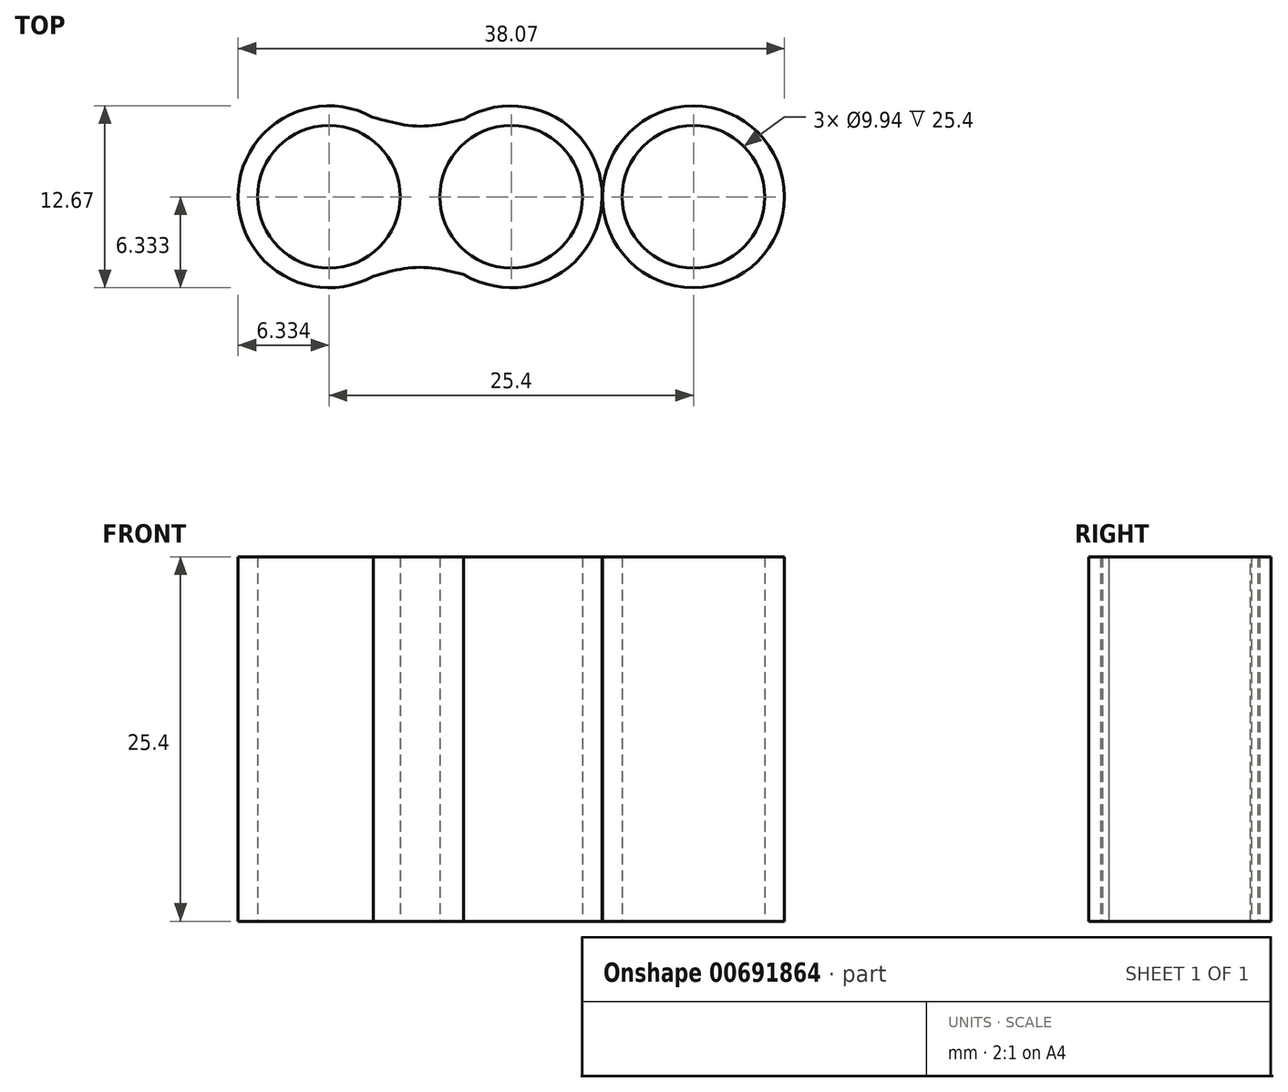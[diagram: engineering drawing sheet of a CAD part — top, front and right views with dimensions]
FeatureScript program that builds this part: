
annotation { "Feature Type Name" : "Feature", "Feature Type Description" : "" }
export const myFeature = defineFeature(function(context is Context, id is Id, definition is map)
    precondition{}
    {
        {
            var Q0;
            Q0=qCreatedBy(makeId("Top.planeOp"),FACE);
            var sketch = newSketch(context, id + "F0", { "sketchPlane" : qUnion([Q0])});
            skCircle(sketch, "E0", {"center": v(-40.64, 31.28) * mm, "radius": 4.97 * mm});
            skCircle(sketch, "E1.1.0.0", {"center": v(-27.94, 31.28) * mm, "radius": 4.97 * mm});
            skCircle(sketch, "E1.2.0.0", {"center": v(-15.24, 31.28) * mm, "radius": 4.97 * mm});
            skLineSegment(sketch, "E1.direction1", {"start": v(-40.64, 31.28) * mm, "end": v(-27.94, 31.28) * mm, "construction": true});
            skCircle(sketch, "E2", {"center": v(-40.64, 31.28) * mm, "radius": 6.34 * mm});
            skCircle(sketch, "E3.1.0.0", {"center": v(-27.94, 31.28) * mm, "radius": 6.34 * mm});
            skCircle(sketch, "E3.2.0.0", {"center": v(-15.24, 31.28) * mm, "radius": 6.34 * mm});
            skFitSpline(sketch, "E4", {"points": [v(-37.6, 36.84) * mm, v(-34.38, 36.2) * mm, v(-31.23, 36.7) * mm], "startDerivative": vector(6.39, -1.85) * mm, "endDerivative": vector(6.33, 1.56) * mm});
            skFitSpline(sketch, "E5", {"points": [v(-24.91, 36.85) * mm, v(-22.1, 35.67) * mm, v(-18.86, 36.47) * mm], "startDerivative": vector(6.39, -1.85) * mm, "endDerivative": vector(6.33, 1.56) * mm});
            skFitSpline(sketch, "E6", {"points": [v(-18.27, 25.72) * mm, v(-21.6, 26.45) * mm, v(-24.84, 25.69) * mm], "startDerivative": vector(-6.14, 2.53) * mm, "endDerivative": vector(-7.82, -3.25) * mm});
            skFitSpline(sketch, "E7", {"points": [v(-31.19, 25.87) * mm, v(-34.43, 26.37) * mm, v(-37.55, 25.75) * mm], "startDerivative": vector(-6.46, 1.58) * mm, "endDerivative": vector(-6.26, -1.83) * mm});
            skSolve(sketch);
        }
        {
            var Q0;
            Q0=makeQuery(id+"F0.imprint","IMPRINT",FACE,{"disambiguationData":[TD([[makeQuery(id+"F0.imprint","IMPRINT",EDGE,{"derivedFrom":sQuery(id+"F0.wireOp",EDGE,"E0")}),-1.0]])]});
            var Q1;
            {var subQ0=sQuery(id+"F0.wireOp",EDGE,"E4");Q1=makeQuery(id+"F0.imprint","IMPRINT",FACE,{"disambiguationData":[TD([[makeQuery(id+"F0.imprint","IMPRINT",EDGE,{"derivedFrom":subQ0}),-1.0]])]});}
            var Q2;
            Q2=makeQuery(id+"F0.imprint","IMPRINT",FACE,{"disambiguationData":[TD([[makeQuery(id+"F0.imprint","IMPRINT",EDGE,{"derivedFrom":sQuery(id+"F0.wireOp",EDGE,"E1.1.0.0")}),-1.0]])]});
            var Q3;
            Q3=makeQuery(id+"F0.imprint","IMPRINT",FACE,{"disambiguationData":[TD([[makeQuery(id+"F0.imprint","IMPRINT",EDGE,{"derivedFrom":sQuery(id+"F0.wireOp",EDGE,"E1.2.0.0")}),-1.0]])]});
            extrude(context, id + "F1", {"entities" : qUnion([Q0, Q1, Q2, Q3]), "depth" : 25.4 * mm, "offsetDistance" : 25.4 * mm});
        }
    });
